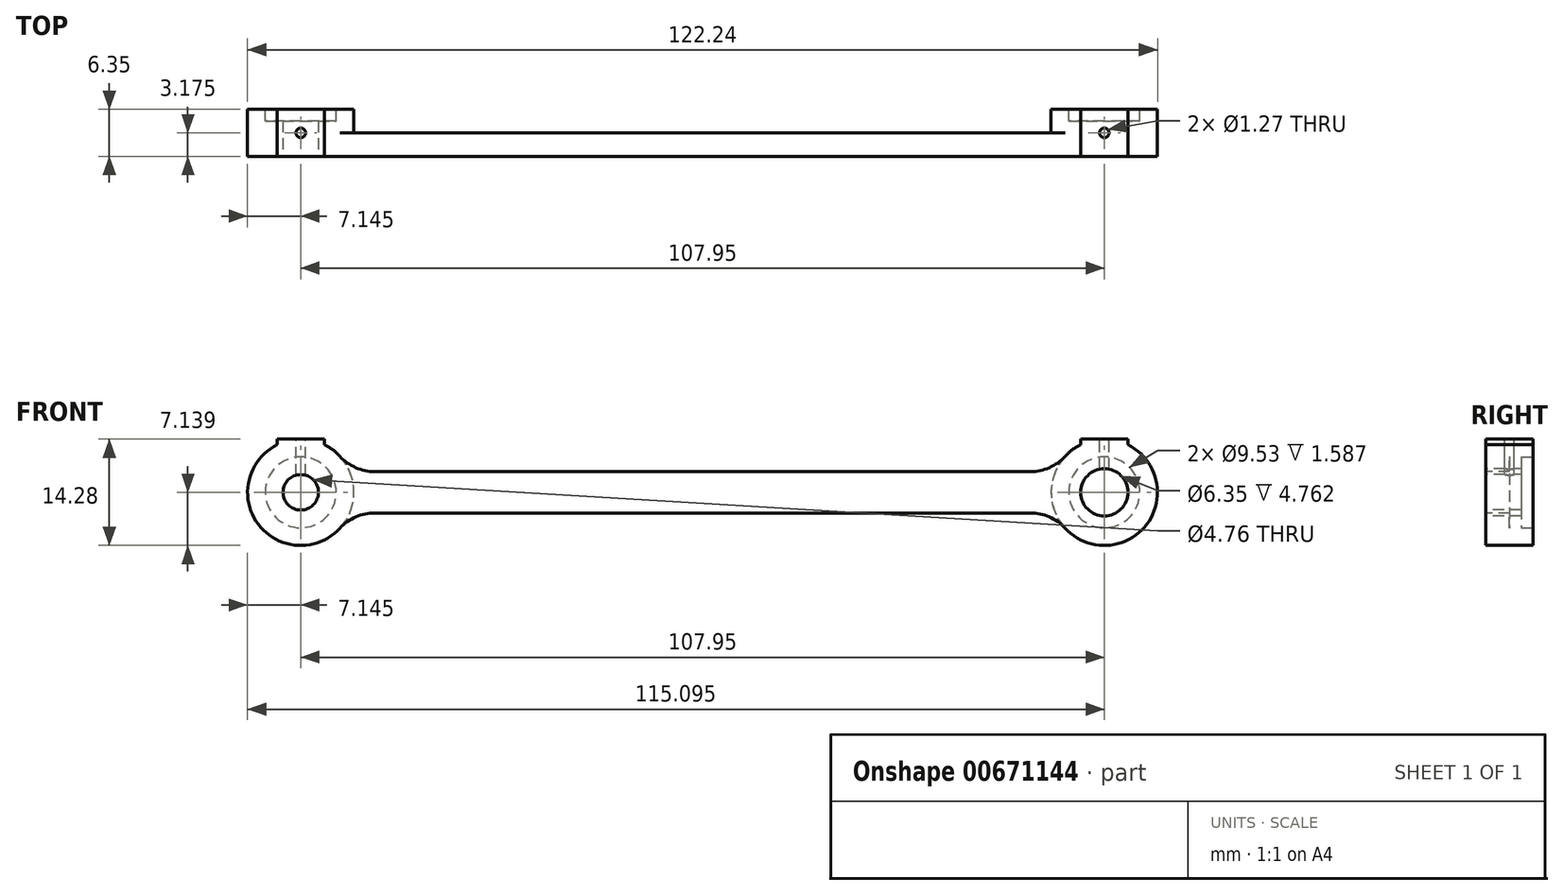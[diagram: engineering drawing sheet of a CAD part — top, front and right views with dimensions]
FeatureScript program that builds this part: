
annotation { "Feature Type Name" : "Feature", "Feature Type Description" : "" }
export const myFeature = defineFeature(function(context is Context, id is Id, definition is map)
    precondition{}
    {
        {
            var Q0;
            Q0=qCreatedBy(makeId("Front.planeOp"),FACE);
            var sketch = newSketch(context, id + "F0", { "sketchPlane" : qUnion([Q0])});
            skLineSegment(sketch, "E0", {"start": v(3.78, 14.91) * mm, "end": v(111.73, 14.91) * mm});
            skLineSegment(sketch, "E1", {"start": v(111.73, 14.91) * mm, "end": v(111.73, 20.47) * mm});
            skLineSegment(sketch, "E2", {"start": v(111.73, 20.47) * mm, "end": v(3.78, 20.47) * mm});
            skLineSegment(sketch, "E3", {"start": v(3.78, 20.47) * mm, "end": v(3.78, 14.91) * mm});
            skSolve(sketch);
        }
        {
            var Q0;
            Q0=qSketchRegion(id+"F0",true);
            extrude(context, id + "F1", {"entities" : qUnion([Q0]), "depth" : 3.17 * mm});
        }
        {
            var Q0;
            Q0=makeQuery(id+"F1.opExtrude","CAP_FACE",FACE,{"disambiguationData":[OSD([sQuery(id+"F0.wireOp",EDGE,"E0"),sQuery(id+"F0.wireOp",EDGE,"E1"),sQuery(id+"F0.wireOp",EDGE,"E2"),sQuery(id+"F0.wireOp",EDGE,"E3")])],"isStart":false});
            var sketch = newSketch(context, id + "F2", { "sketchPlane" : qUnion([Q0])});
            skCircle(sketch, "E4", {"center": v(3.78, 17.69) * mm, "radius": 7.14 * mm});
            skSolve(sketch);
        }
        {
            var Q0;
            Q0=qSketchRegion(id+"F2",true);
            extrude(context, id + "F3", {"entities" : qUnion([Q0]), "operationType" : NewBodyOperationType.ADD, "oppositeDirection" : true, "depth" : 3.17 * mm});
        }
        {
            var Q0;
            Q0=makeQuery(id+"F3.boolean.opBoolean","MERGE",FACE,{"derivedFrom":[makeQuery(id+"F1.opExtrude","CAP_FACE",FACE,{"disambiguationData":[OSD([sQuery(id+"F0.wireOp",EDGE,"E0"),sQuery(id+"F0.wireOp",EDGE,"E1"),sQuery(id+"F0.wireOp",EDGE,"E2"),sQuery(id+"F0.wireOp",EDGE,"E3")])],"isStart":false}),makeQuery(id+"F3.opExtrude","CAP_FACE",FACE,{"disambiguationData":[OSD([sQuery(id+"F2.wireOp",EDGE,"E4")])],"isStart":true})]});
            var sketch = newSketch(context, id + "F4", { "sketchPlane" : qUnion([Q0])});
            skCircle(sketch, "E5", {"center": v(3.78, 17.69) * mm, "radius": 7.14 * mm});
            skSolve(sketch);
        }
        {
            var Q0;
            Q0=qSketchRegion(id+"F4",true);
            extrude(context, id + "F5", {"entities" : qUnion([Q0]), "operationType" : NewBodyOperationType.ADD, "depth" : 3.17 * mm});
        }
        {
            var Q0;
            Q0=makeQuery(id+"F5.opExtrude","CAP_FACE",FACE,{"disambiguationData":[OSD([sQuery(id+"F4.wireOp",EDGE,"E5")])],"isStart":false});
            var sketch = newSketch(context, id + "F6", { "sketchPlane" : qUnion([Q0])});
            skCircle(sketch, "E6", {"center": v(3.78, 17.69) * mm, "radius": 2.38 * mm});
            skSolve(sketch);
        }
        {
            var Q0;
            Q0=qSketchRegion(id+"F6",true);
            extrude(context, id + "F7", {"entities" : qUnion([Q0]), "operationType" : NewBodyOperationType.REMOVE, "oppositeDirection" : true, "depth" : 25.4 * mm});
        }
        {
            var Q0;
            Q0=makeQuery(id+"F5.opExtrude","CAP_FACE",FACE,{"disambiguationData":[OSD([sQuery(id+"F4.wireOp",EDGE,"E5")])],"isStart":false});
            var sketch = newSketch(context, id + "F8", { "sketchPlane" : qUnion([Q0])});
            skLineSegment(sketch, "E7", {"start": v(-3.24, 24.83) * mm, "end": v(11.05, 24.83) * mm});
            skLineSegment(sketch, "E8", {"start": v(0.6, 24.83) * mm, "end": v(0.6, 24.09) * mm});
            skLineSegment(sketch, "E9", {"start": v(3.78, 17.69) * mm, "end": v(3.78, 24.83) * mm});
            skLineSegment(sketch, "E10", {"start": v(6.96, 24.83) * mm, "end": v(6.96, 24.09) * mm});
            skArc(sketch, "E11", {"start": v(0.6, 24.09) * mm, "mid": v(3.78, 24.83) * mm, "end": v(6.96, 24.09) * mm});
            skSolve(sketch);
        }
        {
            var Q0;
            Q0=qSketchRegion(id+"F8",true);
            extrude(context, id + "F9", {"entities" : qUnion([Q0]), "oppositeDirection" : true, "depth" : 6.35 * mm});
        }
        {
            var Q0;
            {var subQ0=sQuery(id+"F8.wireOp",EDGE,"E7");Q0=makeQuery(id+"F9.opExtrude","SWEPT_FACE",FACE,{"disambiguationData":[OSD([subQ0]),TDD([makeQuery(id+"F8.imprint","IMPRINT",EDGE,{"disambiguationData":[TD([[makeQuery(id+"F8.imprint","INTERSECT",VERTEX,{"derivedFrom":[subQ0,sQuery(id+"F8.wireOp",EDGE,"E8")]}),-1.0]])],"derivedFrom":subQ0})])]});}
            var sketch = newSketch(context, id + "F10", { "sketchPlane" : qUnion([Q0])});
            skCircle(sketch, "E12", {"center": v(3.78, -3.17) * mm, "radius": 0.64 * mm});
            skSolve(sketch);
        }
        {
            var Q0;
            Q0=makeQuery(id+"F1.opExtrude","SWEPT_BODY",BODY,{"disambiguationData":[OSD([sQuery(id+"F0.wireOp",EDGE,"E0"),sQuery(id+"F0.wireOp",EDGE,"E1"),sQuery(id+"F0.wireOp",EDGE,"E2"),sQuery(id+"F0.wireOp",EDGE,"E3")])]});
            var Q1;
            Q1=makeQuery(id+"F9.opExtrude","SWEPT_BODY",BODY,{"disambiguationData":[OSD([sQuery(id+"F8.wireOp",EDGE,"E7"),sQuery(id+"F8.wireOp",EDGE,"E8"),sQuery(id+"F8.wireOp",EDGE,"E11")])]});
            var Q2;
            Q2=makeQuery(id+"F9.opExtrude","SWEPT_BODY",BODY,{"disambiguationData":[OSD([sQuery(id+"F8.wireOp",EDGE,"E7"),sQuery(id+"F8.wireOp",EDGE,"E10"),sQuery(id+"F8.wireOp",EDGE,"E11")])]});
            booleanBodies(context, id + "F11", {"operationType" : BooleanOperationType.UNION, "tools" : qUnion([Q0, Q1, Q2])});
        }
        {
            var Q0;
            {var subQ0=sQuery(id+"F10.wireOp",EDGE,"E12");var subQ1=sQuery(id+"F8.wireOp",EDGE,"E11");var subQ2=sQuery(id+"F8.wireOp",EDGE,"E7");var subQ3=makeQuery(id+"F9.opExtrude","SWEPT_EDGE",EDGE,{"disambiguationData":[OSD([subQ2,subQ1]),ownerDisambiguation([makeQuery(id+"F9.opExtrude","SWEPT_BODY",BODY,{"disambiguationData":[OSD([subQ2,sQuery(id+"F8.wireOp",EDGE,"E8"),subQ1])]})])]});var subQ4=makeQuery(id+"F10.imprint","INTERSECT",VERTEX,{"disambiguationData":[OD(0.0)],"derivedFrom":[subQ3,subQ0]});Q0=makeQuery(id+"F10.imprint","IMPRINT",FACE,{"disambiguationData":[TD([[makeQuery(id+"F10.imprint","IMPRINT",EDGE,{"disambiguationData":[TD([[subQ4,1.0]])],"derivedFrom":subQ0}),1.0]])]});}
            var Q1;
            {var subQ0=sQuery(id+"F10.wireOp",EDGE,"E12");var subQ1=sQuery(id+"F8.wireOp",EDGE,"E11");var subQ2=sQuery(id+"F8.wireOp",EDGE,"E7");var subQ3=makeQuery(id+"F9.opExtrude","SWEPT_EDGE",EDGE,{"disambiguationData":[OSD([subQ2,subQ1]),ownerDisambiguation([makeQuery(id+"F9.opExtrude","SWEPT_BODY",BODY,{"disambiguationData":[OSD([subQ2,sQuery(id+"F8.wireOp",EDGE,"E8"),subQ1])]})])]});var subQ4=makeQuery(id+"F10.imprint","INTERSECT",VERTEX,{"disambiguationData":[OD(0.0)],"derivedFrom":[subQ3,subQ0]});Q1=makeQuery(id+"F10.imprint","IMPRINT",FACE,{"disambiguationData":[TD([[makeQuery(id+"F10.imprint","IMPRINT",EDGE,{"disambiguationData":[TD([[subQ4,-1.0]])],"derivedFrom":subQ0}),1.0]])]});}
            extrude(context, id + "F12", {"entities" : qUnion([Q0, Q1]), "operationType" : NewBodyOperationType.REMOVE, "oppositeDirection" : true, "depth" : 6.35 * mm});
        }
        {
            var Q0;
            Q0=makeQuery(id+"F3.boolean.opBoolean","MERGE",FACE,{"derivedFrom":[makeQuery(id+"F1.opExtrude","CAP_FACE",FACE,{"disambiguationData":[OSD([sQuery(id+"F0.wireOp",EDGE,"E0"),sQuery(id+"F0.wireOp",EDGE,"E1"),sQuery(id+"F0.wireOp",EDGE,"E2"),sQuery(id+"F0.wireOp",EDGE,"E3")])],"isStart":false}),makeQuery(id+"F3.opExtrude","CAP_FACE",FACE,{"disambiguationData":[OSD([sQuery(id+"F2.wireOp",EDGE,"E4")])],"isStart":true})]});
            var sketch = newSketch(context, id + "F13", { "sketchPlane" : qUnion([Q0])});
            skCircle(sketch, "E13", {"center": v(111.73, 17.69) * mm, "radius": 7.14 * mm});
            skSolve(sketch);
        }
        {
            var Q0;
            Q0=qSketchRegion(id+"F13",true);
            extrude(context, id + "F14", {"entities" : qUnion([Q0]), "operationType" : NewBodyOperationType.ADD, "oppositeDirection" : true, "depth" : 3.17 * mm});
        }
        {
            var Q0;
            Q0=makeQuery(id+"F14.boolean.opBoolean","MERGE",FACE,{"derivedFrom":[makeQuery(id+"F3.boolean.opBoolean","MERGE",FACE,{"derivedFrom":[makeQuery(id+"F1.opExtrude","CAP_FACE",FACE,{"disambiguationData":[OSD([sQuery(id+"F0.wireOp",EDGE,"E0"),sQuery(id+"F0.wireOp",EDGE,"E1"),sQuery(id+"F0.wireOp",EDGE,"E2"),sQuery(id+"F0.wireOp",EDGE,"E3")])],"isStart":false}),makeQuery(id+"F3.opExtrude","CAP_FACE",FACE,{"disambiguationData":[OSD([sQuery(id+"F2.wireOp",EDGE,"E4")])],"isStart":true})]}),makeQuery(id+"F14.opExtrude","CAP_FACE",FACE,{"disambiguationData":[OSD([sQuery(id+"F13.wireOp",EDGE,"E13")])],"isStart":true})]});
            var sketch = newSketch(context, id + "F15", { "sketchPlane" : qUnion([Q0])});
            skCircle(sketch, "E14", {"center": v(111.73, 17.69) * mm, "radius": 7.14 * mm});
            skSolve(sketch);
        }
        {
            var Q0;
            Q0=qSketchRegion(id+"F15",true);
            extrude(context, id + "F16", {"entities" : qUnion([Q0]), "operationType" : NewBodyOperationType.ADD, "depth" : 3.17 * mm});
        }
        {
            var Q0;
            Q0=makeQuery(id+"F16.opExtrude","CAP_FACE",FACE,{"disambiguationData":[OSD([sQuery(id+"F15.wireOp",EDGE,"E14")])],"isStart":false});
            var sketch = newSketch(context, id + "F17", { "sketchPlane" : qUnion([Q0])});
            skCircle(sketch, "E15", {"center": v(111.73, 17.69) * mm, "radius": 3.18 * mm});
            skSolve(sketch);
        }
        {
            var Q0;
            Q0=qSketchRegion(id+"F17",true);
            extrude(context, id + "F18", {"entities" : qUnion([Q0]), "operationType" : NewBodyOperationType.REMOVE, "oppositeDirection" : true, "depth" : 25.4 * mm});
        }
        {
            var Q0;
            Q0=makeQuery(id+"F16.opExtrude","CAP_FACE",FACE,{"disambiguationData":[OSD([sQuery(id+"F15.wireOp",EDGE,"E14")])],"isStart":false});
            var sketch = newSketch(context, id + "F19", { "sketchPlane" : qUnion([Q0])});
            skLineSegment(sketch, "E16", {"start": v(103.62, 24.83) * mm, "end": v(118.22, 24.83) * mm});
            skLineSegment(sketch, "E17", {"start": v(108.56, 24.83) * mm, "end": v(108.56, 24.09) * mm});
            skLineSegment(sketch, "E18", {"start": v(114.9, 24.83) * mm, "end": v(114.9, 24.09) * mm});
            skLineSegment(sketch, "E19", {"start": v(111.73, 17.69) * mm, "end": v(111.73, 24.83) * mm});
            skArc(sketch, "E20", {"start": v(108.56, 24.09) * mm, "mid": v(111.73, 24.83) * mm, "end": v(114.9, 24.09) * mm});
            skSolve(sketch);
        }
        {
            var Q0;
            Q0=qSketchRegion(id+"F19",true);
            extrude(context, id + "F20", {"entities" : qUnion([Q0]), "operationType" : NewBodyOperationType.ADD, "oppositeDirection" : true, "depth" : 6.35 * mm});
        }
        {
            var Q0;
            {var subQ0=sQuery(id+"F19.wireOp",EDGE,"E16");Q0=makeQuery(id+"F20.boolean.opBoolean","MERGE",FACE,{"derivedFrom":[makeQuery(id+"F20.opExtrude","SWEPT_FACE",FACE,{"disambiguationData":[OSD([subQ0]),TDD([makeQuery(id+"F19.imprint","IMPRINT",EDGE,{"disambiguationData":[TD([[makeQuery(id+"F19.imprint","INTERSECT",VERTEX,{"derivedFrom":[subQ0,sQuery(id+"F19.wireOp",EDGE,"E17")]}),-1.0]])],"derivedFrom":subQ0})])]}),makeQuery(id+"F20.opExtrude","SWEPT_FACE",FACE,{"disambiguationData":[OSD([subQ0]),TDD([makeQuery(id+"F19.imprint","IMPRINT",EDGE,{"disambiguationData":[TD([[makeQuery(id+"F19.imprint","INTERSECT",VERTEX,{"derivedFrom":[subQ0,sQuery(id+"F19.wireOp",EDGE,"E18")]}),1.0]])],"derivedFrom":subQ0})])]})]});}
            var sketch = newSketch(context, id + "F21", { "sketchPlane" : qUnion([Q0])});
            skCircle(sketch, "E21", {"center": v(111.73, -3.18) * mm, "radius": 0.64 * mm});
            skSolve(sketch);
        }
        {
            var Q0;
            Q0=qSketchRegion(id+"F21",true);
            extrude(context, id + "F22", {"entities" : qUnion([Q0]), "operationType" : NewBodyOperationType.REMOVE, "oppositeDirection" : true, "depth" : 6.35 * mm});
        }
        {
            var Q0;
            Q0=makeQuery(id+"F3.boolean.opBoolean","INTERSECT",EDGE,{"derivedFrom":[makeQuery(id+"F1.opExtrude","SWEPT_FACE",FACE,{"disambiguationData":[OSD([sQuery(id+"F0.wireOp",EDGE,"E2")])]}),makeQuery(id+"F3.opExtrude","SWEPT_FACE",FACE,{"disambiguationData":[OSD([sQuery(id+"F2.wireOp",EDGE,"E4")])]})]});
            var Q1;
            Q1=makeQuery(id+"F3.boolean.opBoolean","INTERSECT",EDGE,{"derivedFrom":[makeQuery(id+"F1.opExtrude","SWEPT_FACE",FACE,{"disambiguationData":[OSD([sQuery(id+"F0.wireOp",EDGE,"E0")])]}),makeQuery(id+"F3.opExtrude","SWEPT_FACE",FACE,{"disambiguationData":[OSD([sQuery(id+"F2.wireOp",EDGE,"E4")])]})]});
            var Q2;
            Q2=makeQuery(id+"F14.boolean.opBoolean","INTERSECT",EDGE,{"derivedFrom":[makeQuery(id+"F1.opExtrude","SWEPT_FACE",FACE,{"disambiguationData":[OSD([sQuery(id+"F0.wireOp",EDGE,"E2")])]}),makeQuery(id+"F14.opExtrude","SWEPT_FACE",FACE,{"disambiguationData":[OSD([sQuery(id+"F13.wireOp",EDGE,"E13")])]})]});
            var Q3;
            Q3=makeQuery(id+"F14.boolean.opBoolean","INTERSECT",EDGE,{"derivedFrom":[makeQuery(id+"F1.opExtrude","SWEPT_FACE",FACE,{"disambiguationData":[OSD([sQuery(id+"F0.wireOp",EDGE,"E0")])]}),makeQuery(id+"F14.opExtrude","SWEPT_FACE",FACE,{"disambiguationData":[OSD([sQuery(id+"F13.wireOp",EDGE,"E13")])]})]});
            var Q4;
            Q4=makeQuery(id+"F9.opExtrude","SWEPT_EDGE",EDGE,{"disambiguationData":[OSD([sQuery(id+"F4.wireOp",EDGE,"E5"),sQuery(id+"F8.wireOp",EDGE,"E10"),sQuery(id+"F8.wireOp",EDGE,"E11")])]});
            var Q5;
            Q5=makeQuery(id+"F9.opExtrude","SWEPT_EDGE",EDGE,{"disambiguationData":[OSD([sQuery(id+"F4.wireOp",EDGE,"E5"),sQuery(id+"F8.wireOp",EDGE,"E8"),sQuery(id+"F8.wireOp",EDGE,"E11")])]});
            var Q6;
            Q6=makeQuery(id+"F20.opExtrude","SWEPT_EDGE",EDGE,{"disambiguationData":[OSD([sQuery(id+"F15.wireOp",EDGE,"E14"),sQuery(id+"F19.wireOp",EDGE,"E17"),sQuery(id+"F19.wireOp",EDGE,"E20")])]});
            var Q7;
            Q7=makeQuery(id+"F20.opExtrude","SWEPT_EDGE",EDGE,{"disambiguationData":[OSD([sQuery(id+"F15.wireOp",EDGE,"E14"),sQuery(id+"F19.wireOp",EDGE,"E18"),sQuery(id+"F19.wireOp",EDGE,"E20")])]});
            fillet(context, id + "F23", {"entities" : qUnion([Q0, Q1, Q2, Q3, Q4, Q5, Q6, Q7]), "radius" : 6.35 * mm, "tangentPropagation" : true, "allowEdgeOverflow" : false});
        }
        {
            var Q0;
            Q0=makeQuery(id+"F14.boolean.opBoolean","MERGE",FACE,{"derivedFrom":[makeQuery(id+"F3.boolean.opBoolean","MERGE",FACE,{"derivedFrom":[makeQuery(id+"F1.opExtrude","CAP_FACE",FACE,{"disambiguationData":[OSD([sQuery(id+"F0.wireOp",EDGE,"E0"),sQuery(id+"F0.wireOp",EDGE,"E1"),sQuery(id+"F0.wireOp",EDGE,"E2"),sQuery(id+"F0.wireOp",EDGE,"E3")])],"isStart":false}),makeQuery(id+"F3.opExtrude","CAP_FACE",FACE,{"disambiguationData":[OSD([sQuery(id+"F2.wireOp",EDGE,"E4")])],"isStart":true})]}),makeQuery(id+"F14.opExtrude","CAP_FACE",FACE,{"disambiguationData":[OSD([sQuery(id+"F13.wireOp",EDGE,"E13")])],"isStart":true})]});
            extrude(context, id + "F24", {"entities" : qUnion([Q0]), "operationType" : NewBodyOperationType.ADD, "depth" : 3.17 * mm});
        }
        {
            var Q0;
            {var subQ0=sQuery(id+"F19.wireOp",EDGE,"E20");var subQ1=sQuery(id+"F19.wireOp",EDGE,"E16");var subQ2=sQuery(id+"F8.wireOp",EDGE,"E11");var subQ3=sQuery(id+"F8.wireOp",EDGE,"E7");Q0=makeQuery(id+"F20.boolean.opBoolean","MERGE",FACE,{"derivedFrom":[makeQuery(id+"F14.boolean.opBoolean","MERGE",FACE,{"derivedFrom":[makeQuery(id+"F11.opBoolean","MERGE",FACE,{"derivedFrom":[makeQuery(id+"F3.boolean.opBoolean","MERGE",FACE,{"derivedFrom":[makeQuery(id+"F1.opExtrude","CAP_FACE",FACE,{"disambiguationData":[OSD([sQuery(id+"F0.wireOp",EDGE,"E0"),sQuery(id+"F0.wireOp",EDGE,"E1"),sQuery(id+"F0.wireOp",EDGE,"E2"),sQuery(id+"F0.wireOp",EDGE,"E3")])],"isStart":true}),makeQuery(id+"F3.opExtrude","CAP_FACE",FACE,{"disambiguationData":[OSD([sQuery(id+"F2.wireOp",EDGE,"E4")])],"isStart":false})]}),makeQuery(id+"F9.opExtrude","CAP_FACE",FACE,{"disambiguationData":[OSD([subQ3,sQuery(id+"F8.wireOp",EDGE,"E8"),subQ2])],"isStart":false}),makeQuery(id+"F9.opExtrude","CAP_FACE",FACE,{"disambiguationData":[OSD([subQ3,sQuery(id+"F8.wireOp",EDGE,"E10"),subQ2])],"isStart":false})]}),makeQuery(id+"F14.opExtrude","CAP_FACE",FACE,{"disambiguationData":[OSD([sQuery(id+"F13.wireOp",EDGE,"E13")])],"isStart":false})]}),makeQuery(id+"F20.opExtrude","CAP_FACE",FACE,{"disambiguationData":[OSD([subQ1,sQuery(id+"F19.wireOp",EDGE,"E17"),subQ0])],"isStart":false}),makeQuery(id+"F20.opExtrude","CAP_FACE",FACE,{"disambiguationData":[OSD([subQ1,sQuery(id+"F19.wireOp",EDGE,"E18"),subQ0])],"isStart":false})]});}
            var sketch = newSketch(context, id + "F25", { "sketchPlane" : qUnion([Q0])});
            skArc(sketch, "E22", {"start": v(-9.05, 12.86) * mm, "mid": v(-10.91, 18.16) * mm, "end": v(-8.37, 23.17) * mm});
            skArc(sketch, "E23", {"start": v(-107.15, 23.17) * mm, "mid": v(-104.6, 18.16) * mm, "end": v(-106.47, 12.86) * mm});
            skSolve(sketch);
        }
        {
            var Q0;
            {var subQ15=sQuery(id+"F0.wireOp",EDGE,"E0");Q0=makeQuery(id+"F25.imprint","IMPRINT",FACE,{"disambiguationData":[TD([[makeQuery(id+"F25.imprint","IMPRINT",EDGE,{"derivedFrom":makeQuery(id+"F1.opExtrude","CAP_EDGE",EDGE,{"disambiguationData":[OSD([subQ15])],"isStart":true})}),-1.0]])]});}
            extrude(context, id + "F26", {"entities" : qUnion([Q0]), "operationType" : NewBodyOperationType.REMOVE, "oppositeDirection" : true, "depth" : 3.17 * mm});
        }
        {
            var Q0;
            {var subQ0=sQuery(id+"F8.wireOp",EDGE,"E8");var subQ1=sQuery(id+"F8.wireOp",EDGE,"E7");var subQ2=sQuery(id+"F8.wireOp",EDGE,"E11");var subQ5=sQuery(id+"F8.wireOp",EDGE,"E10");var subQ6=sQuery(id+"F2.wireOp",EDGE,"E4");var subQ7=sQuery(id+"F19.wireOp",EDGE,"E20");var subQ8=sQuery(id+"F19.wireOp",EDGE,"E16");Q0=makeQuery(id+"F26.boolean.opBoolean","SPLIT",FACE,{"disambiguationData":[TD([makeQuery(id+"F3.opExtrude","SWEPT_FACE",FACE,{"disambiguationData":[OSD([subQ6])]})])],"derivedFrom":makeQuery(id+"F20.boolean.opBoolean","MERGE",FACE,{"derivedFrom":[makeQuery(id+"F14.boolean.opBoolean","MERGE",FACE,{"derivedFrom":[makeQuery(id+"F11.opBoolean","MERGE",FACE,{"derivedFrom":[makeQuery(id+"F3.boolean.opBoolean","MERGE",FACE,{"derivedFrom":[makeQuery(id+"F1.opExtrude","CAP_FACE",FACE,{"disambiguationData":[OSD([sQuery(id+"F0.wireOp",EDGE,"E0"),sQuery(id+"F0.wireOp",EDGE,"E1"),sQuery(id+"F0.wireOp",EDGE,"E2"),sQuery(id+"F0.wireOp",EDGE,"E3")])],"isStart":true}),makeQuery(id+"F3.opExtrude","CAP_FACE",FACE,{"disambiguationData":[OSD([subQ6])],"isStart":false})]}),makeQuery(id+"F9.opExtrude","CAP_FACE",FACE,{"disambiguationData":[OSD([subQ1,subQ0,subQ2])],"isStart":false}),makeQuery(id+"F9.opExtrude","CAP_FACE",FACE,{"disambiguationData":[OSD([subQ1,subQ5,subQ2])],"isStart":false})]}),makeQuery(id+"F14.opExtrude","CAP_FACE",FACE,{"disambiguationData":[OSD([sQuery(id+"F13.wireOp",EDGE,"E13")])],"isStart":false})]}),makeQuery(id+"F20.opExtrude","CAP_FACE",FACE,{"disambiguationData":[OSD([subQ8,sQuery(id+"F19.wireOp",EDGE,"E17"),subQ7])],"isStart":false}),makeQuery(id+"F20.opExtrude","CAP_FACE",FACE,{"disambiguationData":[OSD([subQ8,sQuery(id+"F19.wireOp",EDGE,"E18"),subQ7])],"isStart":false})]})});}
            var sketch = newSketch(context, id + "F27", { "sketchPlane" : qUnion([Q0])});
            skCircle(sketch, "E24", {"center": v(-3.78, 17.69) * mm, "radius": 4.76 * mm});
            skSolve(sketch);
        }
        {
            var Q0;
            Q0=qSketchRegion(id+"F27",true);
            extrude(context, id + "F28", {"entities" : qUnion([Q0]), "operationType" : NewBodyOperationType.REMOVE, "oppositeDirection" : true, "depth" : 1.59 * mm});
        }
        {
            var Q0;
            {var subQ0=sQuery(id+"F19.wireOp",EDGE,"E17");var subQ1=sQuery(id+"F19.wireOp",EDGE,"E16");var subQ2=sQuery(id+"F19.wireOp",EDGE,"E20");var subQ5=sQuery(id+"F13.wireOp",EDGE,"E13");var subQ6=sQuery(id+"F19.wireOp",EDGE,"E18");var subQ7=sQuery(id+"F8.wireOp",EDGE,"E11");var subQ8=sQuery(id+"F8.wireOp",EDGE,"E7");Q0=makeQuery(id+"F26.boolean.opBoolean","SPLIT",FACE,{"disambiguationData":[TD([makeQuery(id+"F14.opExtrude","SWEPT_FACE",FACE,{"disambiguationData":[OSD([subQ5])]})])],"derivedFrom":makeQuery(id+"F20.boolean.opBoolean","MERGE",FACE,{"derivedFrom":[makeQuery(id+"F14.boolean.opBoolean","MERGE",FACE,{"derivedFrom":[makeQuery(id+"F11.opBoolean","MERGE",FACE,{"derivedFrom":[makeQuery(id+"F3.boolean.opBoolean","MERGE",FACE,{"derivedFrom":[makeQuery(id+"F1.opExtrude","CAP_FACE",FACE,{"disambiguationData":[OSD([sQuery(id+"F0.wireOp",EDGE,"E0"),sQuery(id+"F0.wireOp",EDGE,"E1"),sQuery(id+"F0.wireOp",EDGE,"E2"),sQuery(id+"F0.wireOp",EDGE,"E3")])],"isStart":true}),makeQuery(id+"F3.opExtrude","CAP_FACE",FACE,{"disambiguationData":[OSD([sQuery(id+"F2.wireOp",EDGE,"E4")])],"isStart":false})]}),makeQuery(id+"F9.opExtrude","CAP_FACE",FACE,{"disambiguationData":[OSD([subQ8,sQuery(id+"F8.wireOp",EDGE,"E8"),subQ7])],"isStart":false}),makeQuery(id+"F9.opExtrude","CAP_FACE",FACE,{"disambiguationData":[OSD([subQ8,sQuery(id+"F8.wireOp",EDGE,"E10"),subQ7])],"isStart":false})]}),makeQuery(id+"F14.opExtrude","CAP_FACE",FACE,{"disambiguationData":[OSD([subQ5])],"isStart":false})]}),makeQuery(id+"F20.opExtrude","CAP_FACE",FACE,{"disambiguationData":[OSD([subQ1,subQ0,subQ2])],"isStart":false}),makeQuery(id+"F20.opExtrude","CAP_FACE",FACE,{"disambiguationData":[OSD([subQ1,subQ6,subQ2])],"isStart":false})]})});}
            var sketch = newSketch(context, id + "F29", { "sketchPlane" : qUnion([Q0])});
            skCircle(sketch, "E25", {"center": v(-111.73, 17.69) * mm, "radius": 4.76 * mm});
            skSolve(sketch);
        }
        {
            var Q0;
            Q0=qSketchRegion(id+"F29",true);
            extrude(context, id + "F30", {"entities" : qUnion([Q0]), "operationType" : NewBodyOperationType.REMOVE, "oppositeDirection" : true, "depth" : 1.59 * mm});
        }
    });
